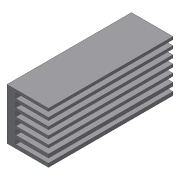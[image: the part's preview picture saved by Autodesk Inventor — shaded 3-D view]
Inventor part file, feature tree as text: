
AUTODESK INVENTOR PART (.ipt)
format: ipt  version: 2018 (Build 220112000, 112)  size: 138,240 bytes
history: native  units: mm
features: extrude x4, sketch x4, projected_geometry x2, mirror x1, pattern_linear x1
ambient origin geometry x8: Origin, YZ Plane, XZ Plane, XY Plane, X Axis, Y Axis, Z Axis, Center Point
bodies: Solid1 (feature_tree)
feature tree (12):
  extrude  "Extrusion1"  Depth=20.0mm
  extrude  "Extrusion2"  Depth=1.7mm
  mirror  "Mirror1"
  extrude  "Extrusion3"  Depth=2.2mm
  pattern_linear  "Rectangular Pattern1"  Spacing1=1.3mm  [1 undecoded]
  extrude  "Extrusion4"  Depth=2.52mm
  sketch  "Sketch1"  dims[d0=20.0mm d1=40.0mm]
  sketch  "Sketch2"  dims[d2=60.0mm d3=0.0mm d4=1.7mm]
  projected_geometry  "Projected Loop1"
  sketch  "Sketch3"  dims[d5=4.2mm d6=2.2mm]
  projected_geometry  "Projected Loop2"
  sketch  "Sketch4"  dims[d7=85.0mm d8=0.0mm d9=1.3mm d10=2.52mm d11=85.0mm d12=0.0mm d13=80.0mm d15=3.82mm d16=10.0mm d17=0.0mm]
note: 1 required parameter value undecoded (feature->parameter linkage not recoverable at this tier; creation-order binding heuristic only, values carry confidence <= 0.55)
